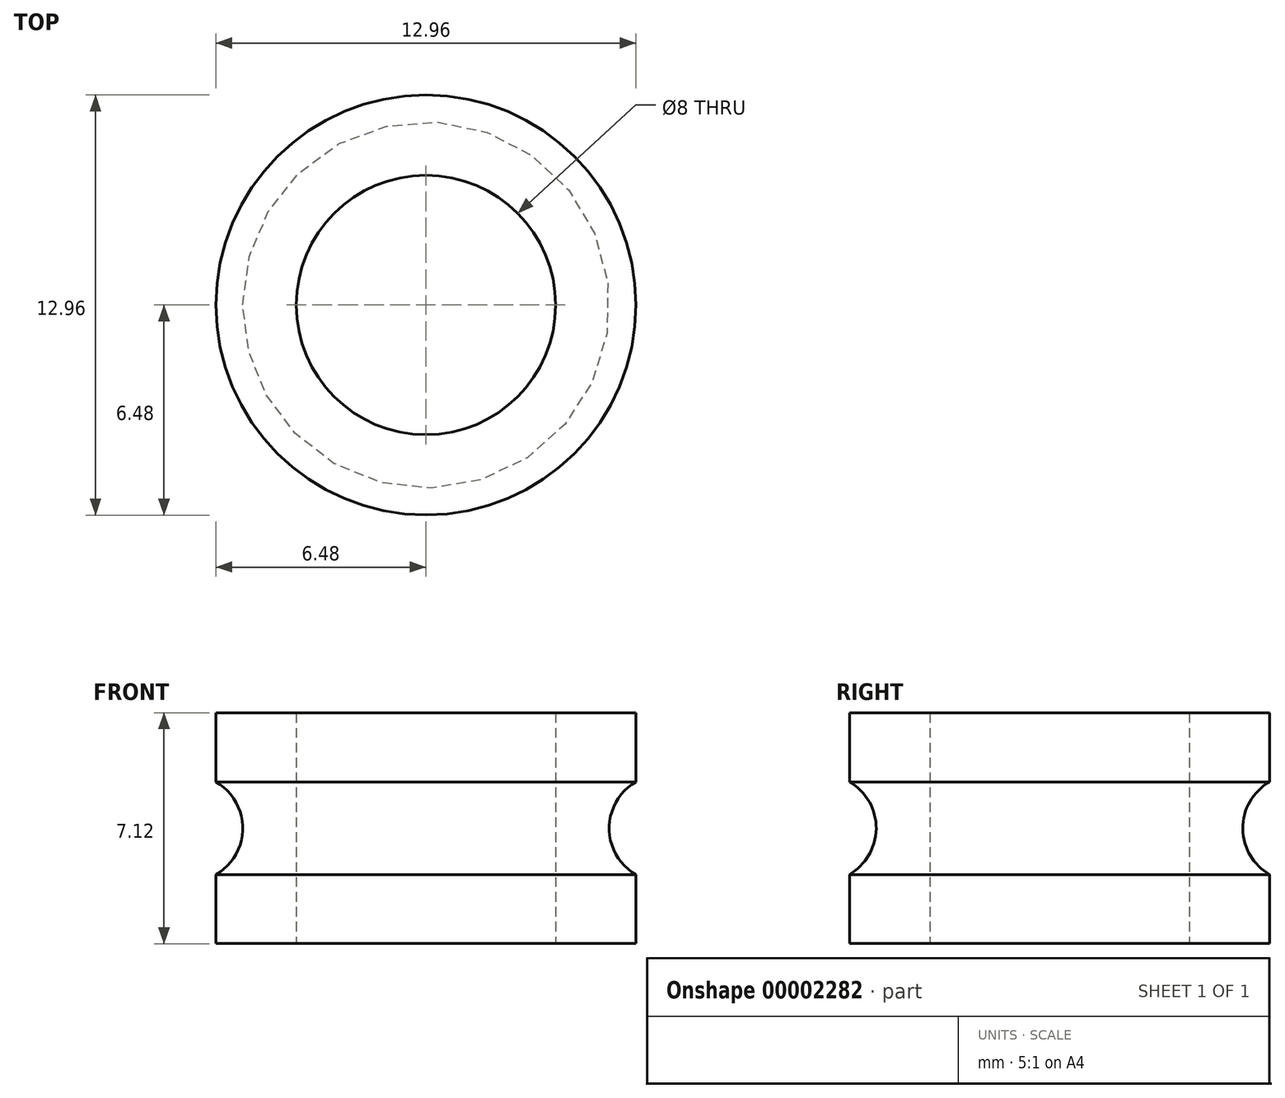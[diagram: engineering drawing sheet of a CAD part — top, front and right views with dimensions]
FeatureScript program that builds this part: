
annotation { "Feature Type Name" : "Feature", "Feature Type Description" : "" }
export const myFeature = defineFeature(function(context is Context, id is Id, definition is map)
    precondition{}
    {
        {
            var Q0;
            Q0=qCreatedBy(makeId("Top.planeOp"),FACE);
            var sketch = newSketch(context, id + "F0", { "sketchPlane" : qUnion([Q0])});
            skCircle(sketch, "E0", {"center": v(0, 0) * mm, "radius": 4 * mm});
            skCircle(sketch, "E1", {"center": v(0, 0) * mm, "radius": 6.48 * mm});
            skSolve(sketch);
        }
        {
            var Q0;
            Q0=makeQuery(id+"F0.imprint","IMPRINT",FACE,{"disambiguationData":[TD([[makeQuery(id+"F0.imprint","IMPRINT",EDGE,{"derivedFrom":sQuery(id+"F0.wireOp",EDGE,"E0")}),-1.0]])]});
            extrude(context, id + "F1", {"entities" : qUnion([Q0]), "endBound" : BoundingType.SYMMETRIC, "depth" : 7.11 * mm});
        }
        {
            var Q0;
            Q0=qCreatedBy(makeId("Front.planeOp"),FACE);
            var sketch = newSketch(context, id + "F2", { "sketchPlane" : qUnion([Q0])});
            skCircle(sketch, "E2", {"center": v(7.3, 0) * mm, "radius": 1.65 * mm});
            skLineSegment(sketch, "E3", {"start": v(0, 0) * mm, "end": v(0, -4.56) * mm, "construction": true});
            skSolve(sketch);
        }
        {
            var Q0;
            Q0=makeQuery(id+"F2.imprint","IMPRINT",FACE,{"disambiguationData":[TD([[makeQuery(id+"F2.imprint","IMPRINT",EDGE,{"derivedFrom":sQuery(id+"F2.wireOp",EDGE,"E2")}),1.0]])]});
            var Q1;
            Q1=sQuery(id+"F2.wireOp",EDGE,"E3");
            revolve(context, id + "F3", {"operationType" : NewBodyOperationType.REMOVE, "entities" : qUnion([Q0]), "axis" : qUnion([Q1]), "revolveType" : RevolveType.FULL, "oppositeDirection" : true});
        }
    });
